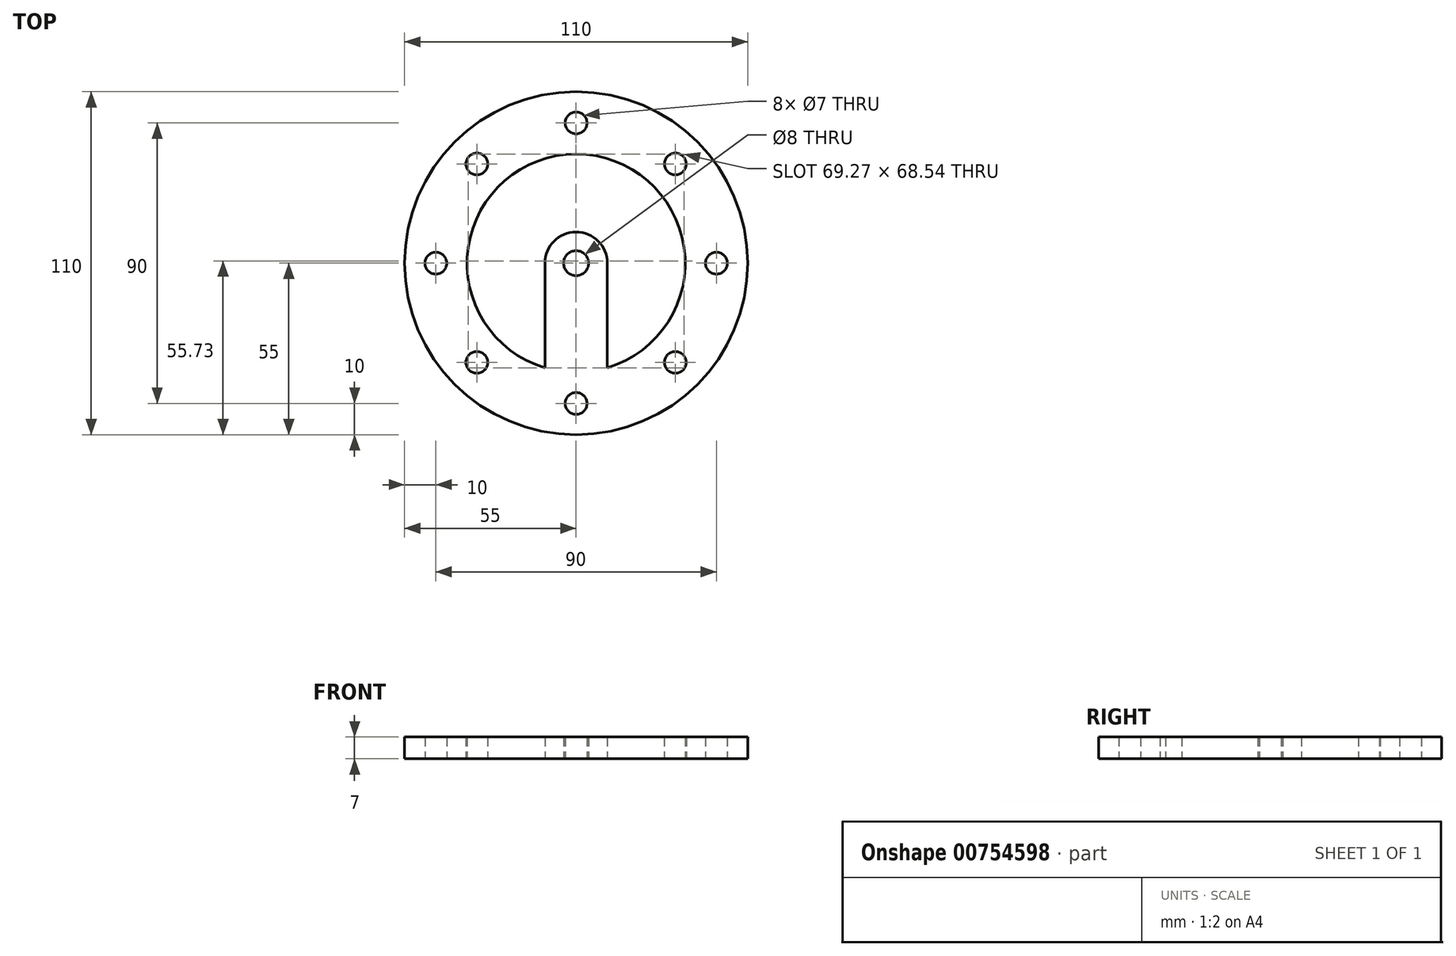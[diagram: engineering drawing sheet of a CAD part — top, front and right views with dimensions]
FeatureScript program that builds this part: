
annotation { "Feature Type Name" : "Feature", "Feature Type Description" : "" }
export const myFeature = defineFeature(function(context is Context, id is Id, definition is map)
    precondition{}
    {
        {
            var Q0;
            Q0=qCreatedBy(makeId("Top.planeOp"),FACE);
            var sketch = newSketch(context, id + "F0", { "sketchPlane" : qUnion([Q0])});
            skCircle(sketch, "E0", {"center": v(0, 0) * mm, "radius": 55 * mm});
            skCircle(sketch, "E1", {"center": v(0, 0) * mm, "radius": 35 * mm});
            skCircle(sketch, "E2", {"center": v(0, 0) * mm, "radius": 45 * mm, "construction": true});
            skPoint(sketch, "E3", {"position": v(-35, 0) * mm});
            skPoint(sketch, "E4", {"position": v(-55, 0) * mm});
            skPoint(sketch, "E5", {"position": v(35, 0) * mm});
            skPoint(sketch, "E6", {"position": v(55, 0) * mm});
            skPoint(sketch, "E7", {"position": v(0, 55) * mm});
            skPoint(sketch, "E8", {"position": v(0, 35) * mm});
            skPoint(sketch, "E9", {"position": v(0, -35) * mm});
            skPoint(sketch, "E10", {"position": v(0, -55) * mm});
            skCircle(sketch, "E11", {"center": v(-45, 0) * mm, "radius": 3.5 * mm});
            skCircle(sketch, "E12", {"center": v(45, 0) * mm, "radius": 3.5 * mm});
            skCircle(sketch, "E13", {"center": v(0, -45) * mm, "radius": 3.5 * mm});
            skCircle(sketch, "E14", {"center": v(0, 45) * mm, "radius": 3.5 * mm});
            skCircle(sketch, "E15", {"center": v(-31.82, 31.82) * mm, "radius": 3.5 * mm});
            skCircle(sketch, "E16", {"center": v(31.82, 31.82) * mm, "radius": 3.5 * mm});
            skCircle(sketch, "E17", {"center": v(31.82, -31.82) * mm, "radius": 3.5 * mm});
            skCircle(sketch, "E18", {"center": v(-31.82, -31.82) * mm, "radius": 3.5 * mm});
            skLineSegment(sketch, "E19", {"start": v(10, 0) * mm, "end": v(-10, 0) * mm, "construction": true});
            skCircle(sketch, "E20", {"center": v(0, 0) * mm, "radius": 10 * mm});
            skCircle(sketch, "E21", {"center": v(0, 0) * mm, "radius": 4 * mm});
            skLineSegment(sketch, "E22", {"start": v(-10, 0) * mm, "end": v(-10, -33.54) * mm});
            skLineSegment(sketch, "E23", {"start": v(10, 0) * mm, "end": v(10, -33.54) * mm});
            skSolve(sketch);
        }
        {
            var Q0;
            Q0 = qSketchRegion(id + "F0", true);
            var Q1;
            Q1=makeQuery(id+"F0.imprint","IMPRINT",FACE,{"disambiguationData":[TD([[makeQuery(id+"F0.imprint","IMPRINT",EDGE,{"derivedFrom":sQuery(id+"F0.wireOp",EDGE,"E21")}),-1.0]])]});
            var Q2;
            {var subQ0=sQuery(id+"F0.wireOp",EDGE,"E22");Q2=makeQuery(id+"F0.imprint","IMPRINT",FACE,{"disambiguationData":[TD([[makeQuery(id+"F0.imprint","IMPRINT",EDGE,{"derivedFrom":subQ0}),1.0]])]});}
            extrude(context, id + "F1", {"entities" : qUnion([Q0, Q1, Q2]), "depth" : 7 * mm, "offsetDistance" : 25 * mm});
        }
    });
